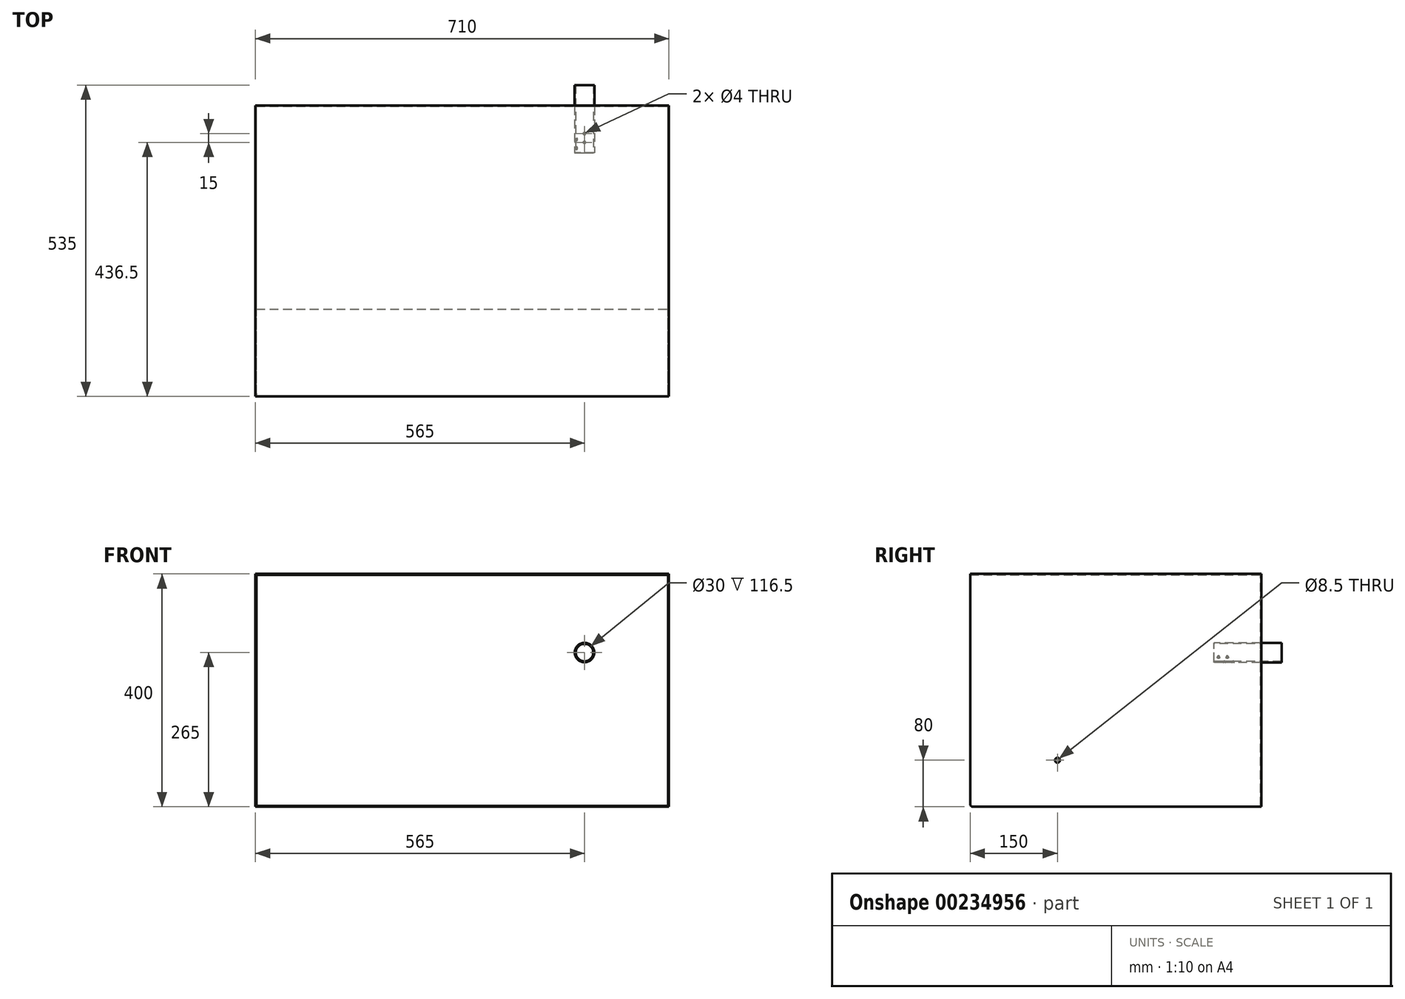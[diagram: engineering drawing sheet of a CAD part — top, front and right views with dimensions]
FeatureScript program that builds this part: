
annotation { "Feature Type Name" : "Feature", "Feature Type Description" : "" }
export const myFeature = defineFeature(function(context is Context, id is Id, definition is map)
    precondition{}
    {
        {
            var Q0;
            Q0=qCreatedBy(makeId("Front.planeOp"),FACE);
            var sketch = newSketch(context, id + "F0", { "sketchPlane" : qUnion([Q0])});
            skLineSegment(sketch, "E0.bottom", {"start": v(-710, 0) * mm, "end": v(0, 0) * mm});
            skLineSegment(sketch, "E0.top", {"start": v(-710, -400) * mm, "end": v(0, -400) * mm});
            skLineSegment(sketch, "E0.left", {"start": v(-710, -400) * mm, "end": v(-710, 0) * mm});
            skLineSegment(sketch, "E0.right", {"start": v(0, -400) * mm, "end": v(0, 0) * mm});
            skSolve(sketch);
        }
        {
            var Q0;
            Q0 = qSketchRegion(id + "F0", true);
            extrude(context, id + "F1", {"entities" : qUnion([Q0]), "depth" : 500 * mm});
        }
        {
            var Q0;
            Q0=makeQuery(id+"F1.opExtrude","CAP_FACE",FACE,{"disambiguationData":[OSD([sQuery(id+"F0.wireOp",EDGE,"E0.bottom"),sQuery(id+"F0.wireOp",EDGE,"E0.top"),sQuery(id+"F0.wireOp",EDGE,"E0.left"),sQuery(id+"F0.wireOp",EDGE,"E0.right")])],"isStart":false});
            shell(context, id + "F2", {"entities" : qUnion([Q0]), "thickness" : 1.5 * mm});
        }
        {
            var Q0;
            Q0=makeQuery(id+"F1.opExtrude","SWEPT_FACE",FACE,{"disambiguationData":[OSD([sQuery(id+"F0.wireOp",EDGE,"E0.top")])]});
            var sketch = newSketch(context, id + "F3", { "sketchPlane" : qUnion([Q0])});
            skLineSegment(sketch, "E1.bottom", {"start": v(-708.5, 500) * mm, "end": v(-1.5, 500) * mm});
            skLineSegment(sketch, "E1.top", {"start": v(-708.5, 350) * mm, "end": v(-1.5, 350) * mm});
            skLineSegment(sketch, "E1.left", {"start": v(-708.5, 500) * mm, "end": v(-708.5, 350) * mm});
            skLineSegment(sketch, "E1.right", {"start": v(-1.5, 500) * mm, "end": v(-1.5, 350) * mm});
            skSolve(sketch);
        }
        {
            var Q0;
            Q0 = qSketchRegion(id + "F3", true);
            extrude(context, id + "F4", {"entities" : qUnion([Q0]), "operationType" : NewBodyOperationType.REMOVE, "endBound" : BoundingType.UP_TO_NEXT, "oppositeDirection" : true, "depth" : 25 * mm});
        }
        {
            var Q0;
            Q0=qCreatedBy(makeId("Top.planeOp"),FACE);
            cPlane(context, id + "F5", {"entities" : qUnion([Q0]), "cplaneType" : CPlaneType.OFFSET, "offset" : 135 * mm, "oppositeDirection" : true, "width" : 150 * mm, "height" : 150 * mm});
        }
        {
            var Q0;
            Q0=qCreatedBy(id+"F5.planeOp",FACE);
            var sketch = newSketch(context, id + "F6", { "sketchPlane" : qUnion([Q0])});
            skLineSegment(sketch, "E2.bottom", {"start": v(-130, -81.5) * mm, "end": v(-128.15, -81.5) * mm});
            skLineSegment(sketch, "E2.top", {"start": v(-130, 35) * mm, "end": v(-128.15, 35) * mm});
            skLineSegment(sketch, "E2.left", {"start": v(-130, -81.5) * mm, "end": v(-130, 35) * mm});
            skLineSegment(sketch, "E2.right", {"start": v(-128.15, -81.5) * mm, "end": v(-128.15, 35) * mm});
            skLineSegment(sketch, "E3", {"start": v(-145, -81.5) * mm, "end": v(-145, 35) * mm});
            skSolve(sketch);
        }
        {
            var Q0;
            Q0=makeQuery(id+"F6.imprint","IMPRINT",FACE,{"disambiguationData":[TD([[makeQuery(id+"F6.imprint","IMPRINT",EDGE,{"derivedFrom":sQuery(id+"F6.wireOp",EDGE,"E2.bottom")}),1.0]])]});
            var Q1;
            Q1=sQuery(id+"F6.wireOp",EDGE,"E3");
            revolve(context, id + "F7", {"operationType" : NewBodyOperationType.ADD, "entities" : qUnion([Q0]), "axis" : qUnion([Q1]), "revolveType" : RevolveType.FULL});
        }
        {
            var Q0;
            Q0=makeQuery(id+"F7.boolean.opBoolean","SPLIT",FACE,{"disambiguationData":[TD([makeQuery(id+"F7.opRevolve","SWEPT_FACE",FACE,{"disambiguationData":[OSD([sQuery(id+"F6.wireOp",EDGE,"E2.left")])]})])],"derivedFrom":makeQuery(id+"F2.opShell","OFFSET_FACE",FACE,{"disambiguationData":[OSD([sQuery(id+"F0.wireOp",EDGE,"E0.bottom"),sQuery(id+"F0.wireOp",EDGE,"E0.top"),sQuery(id+"F0.wireOp",EDGE,"E0.left"),sQuery(id+"F0.wireOp",EDGE,"E0.right")])]})});
            extrude(context, id + "F8", {"entities" : qUnion([Q0]), "operationType" : NewBodyOperationType.REMOVE, "endBound" : BoundingType.THROUGH_ALL, "oppositeDirection" : true, "depth" : 25 * mm});
        }
        {
            var Q0;
            Q0=qCreatedBy(id+"F5.planeOp",FACE);
            var sketch = newSketch(context, id + "F9", { "sketchPlane" : qUnion([Q0])});
            skCircle(sketch, "E4", {"center": v(-145, -63.5) * mm, "radius": 2 * mm});
            skCircle(sketch, "E5", {"center": v(-145, -48.5) * mm, "radius": 2 * mm});
            skSolve(sketch);
        }
        {
            var Q0;
            Q0 = qSketchRegion(id + "F9", true);
            var Q1;
            Q1=makeQuery(id+"F7.boolean.opBoolean","SPLIT",FACE,{"disambiguationData":[TD([makeQuery(id+"F7.opRevolve","SWEPT_FACE",FACE,{"disambiguationData":[OSD([sQuery(id+"F6.wireOp",EDGE,"E2.bottom")])]})])],"derivedFrom":makeQuery(id+"F7.opRevolve","SWEPT_FACE",FACE,{"disambiguationData":[OSD([sQuery(id+"F6.wireOp",EDGE,"E2.right")])]})});
            extrude(context, id + "F10", {"entities" : qUnion([Q0]), "operationType" : NewBodyOperationType.REMOVE, "endBound" : BoundingType.UP_TO_SURFACE, "oppositeDirection" : true, "endBoundEntityFace" : qUnion([Q1]), "depth" : 40 * mm});
        }
        {
            var Q0;
            {var subQ0=sQuery(id+"F6.wireOp",EDGE,"E2.left");var subQ1=sQuery(id+"F0.wireOp",EDGE,"E0.right");var subQ2=sQuery(id+"F0.wireOp",EDGE,"E0.left");var subQ3=sQuery(id+"F0.wireOp",EDGE,"E0.top");var subQ4=sQuery(id+"F0.wireOp",EDGE,"E0.bottom");var subQ5=makeQuery(id+"F7.opRevolve","SWEPT_FACE",FACE,{"disambiguationData":[OSD([subQ0])]});Q0=makeQuery(id+"F8.boolean.opBoolean","MERGE",FACE,{"derivedFrom":[makeQuery(id+"F7.boolean.opBoolean","SPLIT",FACE,{"disambiguationData":[TD([makeQuery(id+"F7.opRevolve","SWEPT_FACE",FACE,{"disambiguationData":[OSD([sQuery(id+"F6.wireOp",EDGE,"E2.bottom")])]})])],"derivedFrom":subQ5}),makeQuery(id+"F7.boolean.opBoolean","SPLIT",FACE,{"disambiguationData":[TD([makeQuery(id+"F7.opRevolve","SWEPT_FACE",FACE,{"disambiguationData":[OSD([sQuery(id+"F6.wireOp",EDGE,"E2.top")])]})])],"derivedFrom":subQ5}),makeQuery(id+"F8.opExtrude","SWEPT_FACE",FACE,{"disambiguationData":[OSD([subQ4,subQ3,subQ2,subQ1,subQ0])]})]});}
            var Q1;
            {var subQ0=sQuery(id+"F0.wireOp",EDGE,"E0.bottom");Q1=makeQuery(id+"F2.opShell","OFFSET_EDGE",EDGE,{"disambiguationData":[OSD([subQ0]),TDD([makeQuery(id+"F1.opExtrude","CAP_EDGE",EDGE,{"disambiguationData":[OSD([subQ0])],"isStart":true})])]});}
            cPlane(context, id + "F11", {"entities" : qUnion([Q0, Q1]), "cplaneType" : CPlaneType.LINE_ANGLE, "offset" : 25 * mm, "angle" : 60 * degree, "width" : 150 * mm, "height" : 150 * mm});
        }
        {
            var Q0;
            Q0=qCreatedBy(id+"F11.planeOp",FACE);
            var sketch = newSketch(context, id + "F12", { "sketchPlane" : qUnion([Q0])});
            skCircle(sketch, "E6", {"center": v(73.5, -44.41) * mm, "radius": 2 * mm});
            skCircle(sketch, "E7", {"center": v(58.5, -44.41) * mm, "radius": 2 * mm});
            skSolve(sketch);
        }
        {
            var Q0;
            Q0 = qSketchRegion(id + "F12", true);
            var Q1;
            Q1=makeQuery(id+"F7.boolean.opBoolean","SPLIT",FACE,{"disambiguationData":[TD([makeQuery(id+"F7.opRevolve","SWEPT_FACE",FACE,{"disambiguationData":[OSD([sQuery(id+"F6.wireOp",EDGE,"E2.bottom")])]})])],"derivedFrom":makeQuery(id+"F7.opRevolve","SWEPT_FACE",FACE,{"disambiguationData":[OSD([sQuery(id+"F6.wireOp",EDGE,"E2.right")])]})});
            extrude(context, id + "F13", {"entities" : qUnion([Q0]), "operationType" : NewBodyOperationType.REMOVE, "endBound" : BoundingType.UP_TO_SURFACE, "endBoundEntityFace" : qUnion([Q1]), "depth" : 25 * mm});
        }
        {
            var Q0;
            Q0=makeQuery(id+"F1.opExtrude","SWEPT_FACE",FACE,{"disambiguationData":[OSD([sQuery(id+"F0.wireOp",EDGE,"E0.right")])]});
            var sketch = newSketch(context, id + "F14", { "sketchPlane" : qUnion([Q0])});
            skCircle(sketch, "E8", {"center": v(-350, -320) * mm, "radius": 4.25 * mm});
            skSolve(sketch);
        }
        {
            var Q0;
            Q0 = qSketchRegion(id + "F14", true);
            extrude(context, id + "F15", {"entities" : qUnion([Q0]), "operationType" : NewBodyOperationType.REMOVE, "endBound" : BoundingType.UP_TO_NEXT, "oppositeDirection" : true, "depth" : 25 * mm});
        }
        {
            var Q0;
            {var subQ0=sQuery(id+"F0.wireOp",EDGE,"E0.right");var subQ1=sQuery(id+"F0.wireOp",EDGE,"E0.top");Q0=makeQuery(id+"F4.boolean.opBoolean","SPLIT",EDGE,{"disambiguationData":[TD([makeQuery(id+"F1.opExtrude","SWEPT_FACE",FACE,{"disambiguationData":[OSD([subQ0])]})])],"derivedFrom":makeQuery(id+"F1.opExtrude","CAP_EDGE",EDGE,{"disambiguationData":[OSD([subQ1])],"isStart":false})});}
            var Q1;
            {var subQ0=sQuery(id+"F0.wireOp",EDGE,"E0.left");var subQ1=sQuery(id+"F0.wireOp",EDGE,"E0.top");Q1=makeQuery(id+"F4.boolean.opBoolean","SPLIT",EDGE,{"disambiguationData":[TD([makeQuery(id+"F1.opExtrude","SWEPT_FACE",FACE,{"disambiguationData":[OSD([subQ0])]})])],"derivedFrom":makeQuery(id+"F1.opExtrude","CAP_EDGE",EDGE,{"disambiguationData":[OSD([subQ1])],"isStart":false})});}
            fillet(context, id + "F16", {"entities" : qUnion([Q0, Q1]), "radius" : 5 * mm, "tangentPropagation" : true, "allowEdgeOverflow" : false});
        }
    });
